# Revit family: Gleitlager T, schallgedämmt, Ø64 bis 219mm
name_source: partatom
category: HLS-Bauteile
revit_build: Autodesk Revit 2018 (Build: 20190510_1515(x64)
units: mm (PartAtom-declared; Revit-internal decimal feet)

## family parameters
Arbeitsebenenbasiert = Ja
Beim Laden mit Abzugskörper schneiden = Nein
Bemaßung runder Anschluss = Durchmesser verwenden
Gemeinsam genutzt = Ja
Immer vertikal = Nein
Klassifizierung = Keine
Raumberechnungspunkt = Nein
Teiletyp = Normal

## types (13) — shared parameters
Baustoffklasse = B2
Breite Schellenband = 50 mm
Breite Unterbau = 100 mm
Dämmstärke = 6 mm  [stored 0.019685 ft]
Fabrikat = MEFA
Höhe Unterbau = 111 mm
Kurztext1 = Gleitlager T h=111 50 x 5 mm
Länge Unterbau = 250 mm
Mengeneinheit = St
Schalldämmeinlage = Gummi EPDM
Sicherheitsfaktor = 1.54
Verschluss-Schraube = M12
Vorgabe-Ansicht = 1219 mm
max. Temperaturbeständigkeit = 100 °C
vpe = 1
zero-valued in all types: Stärke, max. Rohraußendurchmesser, min. Rohraußendurchmesser

## per-type parameters (varying)
| type | Artikelnummer | EAN | Gewicht | Kurztext2 | RS Titan m.D. von Ø64 bis Ø219mm |
| Gleitlager T Ø  64, Gummi | 145fb0064 | 4250928460127 | 6.44 kg | 64 mm EPDM fsv | Rohrschelle Titan HD, o.A., Gummi 30Grad : Titan HD, o.A, Ø64, Gummi |
| Gleitlager T Ø  76, Gummi | 145fb0076 | 4250928460134 | 6.64 kg | 76 mm EPDM fsv | Rohrschelle Titan HD, o.A., Gummi 30Grad : Titan HD, o.A, Ø76, Gummi |
| Gleitlager T Ø  89, Gummi | 145fb0089 | 4250928460141 | 6.87 kg | 89 mm EPDM fsv | Rohrschelle Titan HD, o.A., Gummi 30Grad : Titan HD, o.A, Ø89, Gummi |
| Gleitlager T Ø 108, Gummi | 145fb0108 | 4250928460158 | 7.17 kg | 108 mm EPDM fsv | Rohrschelle Titan HD, o.A., Gummi 30Grad : Titan HD, o.A, Ø108, Gummi |
| Gleitlager T Ø 110, Gummi | 145fb0110 | 4250928460165 | 7.19 kg | 110 mm EPDM fsv | Rohrschelle Titan HD, o.A., Gummi 30Grad : Titan HD, o.A, Ø110, Gummi |
| Gleitlager T Ø 114, Gummi | 145fb0114 | 4250928460172 | 7.26 kg | 114 mm EPDM fsv | Rohrschelle Titan HD, o.A., Gummi 30Grad : Titan HD, o.A, Ø114, Gummi |
| Gleitlager T Ø 133, Gummi | 145fb0133 | 4250928460189 | 7.58 kg | 133 mm EPDM fsv | Rohrschelle Titan HD, o.A., Gummi 30Grad : Titan HD, o.A, Ø133, Gummi |
| Gleitlager T Ø 140, Gummi | 145fb0140 | 4250928460196 | 7.69 kg | 140 mm EPDM fsv | Rohrschelle Titan HD, o.A., Gummi 30Grad : Titan HD, o.A, Ø140, Gummi |
| Gleitlager T Ø 160, Gummi | 145fb0160 | 4250928460202 | 8.02 kg | 160 mm EPDM fsv | Rohrschelle Titan HD, o.A., Gummi 30Grad : Titan HD, o.A, Ø160, Gummi |
| Gleitlager T Ø 168, Gummi | 145fb0168 | 4250928460219 | 8.14 kg | 168 mm EPDM fsv | Rohrschelle Titan HD, o.A., Gummi 30Grad : Titan HD, o.A, Ø168, Gummi |
| Gleitlager T Ø 180, Gummi | 145fb0180 | 4250928460226 | 8.33 kg | 180 mm EPDM fsv | Rohrschelle Titan HD, o.A., Gummi 30Grad : Titan HD, o.A, Ø180, Gummi |
| Gleitlager T Ø 210, Gummi | 145fb0210 | 4250928460233 | 8.81 kg | 210 mm EPDM fsv | Rohrschelle Titan HD, o.A., Gummi 30Grad : Titan HD, o.A, Ø210, Gummi |
| Gleitlager T Ø 219, Gummi | 145fb0219 | 4250928460240 | 8.97 kg | 219 mm EPDM fsv | Rohrschelle Titan HD, o.A., Gummi 30Grad : Titan HD, o.A, Ø219, Gummi |

note: [stored X ft] marks values corroborated as IEEE doubles in the binary element streams (Revit-internal decimal feet)

## geometry (parser evidence)
native form markers: Sweep x4
no freeform markers — native parametric forms only
